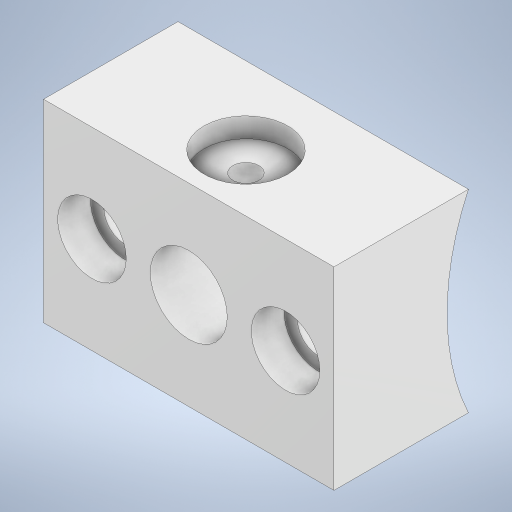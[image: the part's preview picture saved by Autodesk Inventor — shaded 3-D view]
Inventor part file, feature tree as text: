
AUTODESK INVENTOR PART (.ipt)
format: ipt  version: 2023 (Build 270158030, 158C)  size: 257,024 bytes
history: native  units: in
note: dims shown in document units (in); Inventor stores cm internally (conversion verified against a paired STEP export)
features: sketch x4, extrude x2, hole x2
ambient origin geometry x8: Origin, YZ Plane, XZ Plane, XY Plane, X Axis, Y Axis, Z Axis, Center Point
bodies: Solid1 (feature_tree)
feature tree (8):
  extrude  "Extrusion1"  Depth=1.5in TaperAngle=0.0deg
  extrude  "Extrusion6"  Depth=1.0in
  hole  "Hole2"  [1 undecoded]
  hole  "Hole3"  [1 undecoded]
  sketch  "Sketch1"  dims[d0=2.375in d4=1.5in d5=0.0in]
  sketch  "Sketch8"  dims[d47=1.7717in d48=1.0in]
  sketch  "Sketch10"  dims[d49=0.3976in d50=0.0in d51=0.0in]
  sketch  "Sketch11"  dims[d52=0.1339in d53=0.2362in d54=0.4331in d55=0.1024in d56=0.5635in d57=0.315in d58=0.8108in d60=0.2953in d61=0.2165in d62=0.2362in d63=0.3543in d64=0.1693in d65=90.0deg d66=0.315in d67=0.8108in d68=1.0in]
note: 2 required parameter values undecoded (feature->parameter linkage not recoverable at this tier; creation-order binding heuristic only, values carry confidence <= 0.55)
